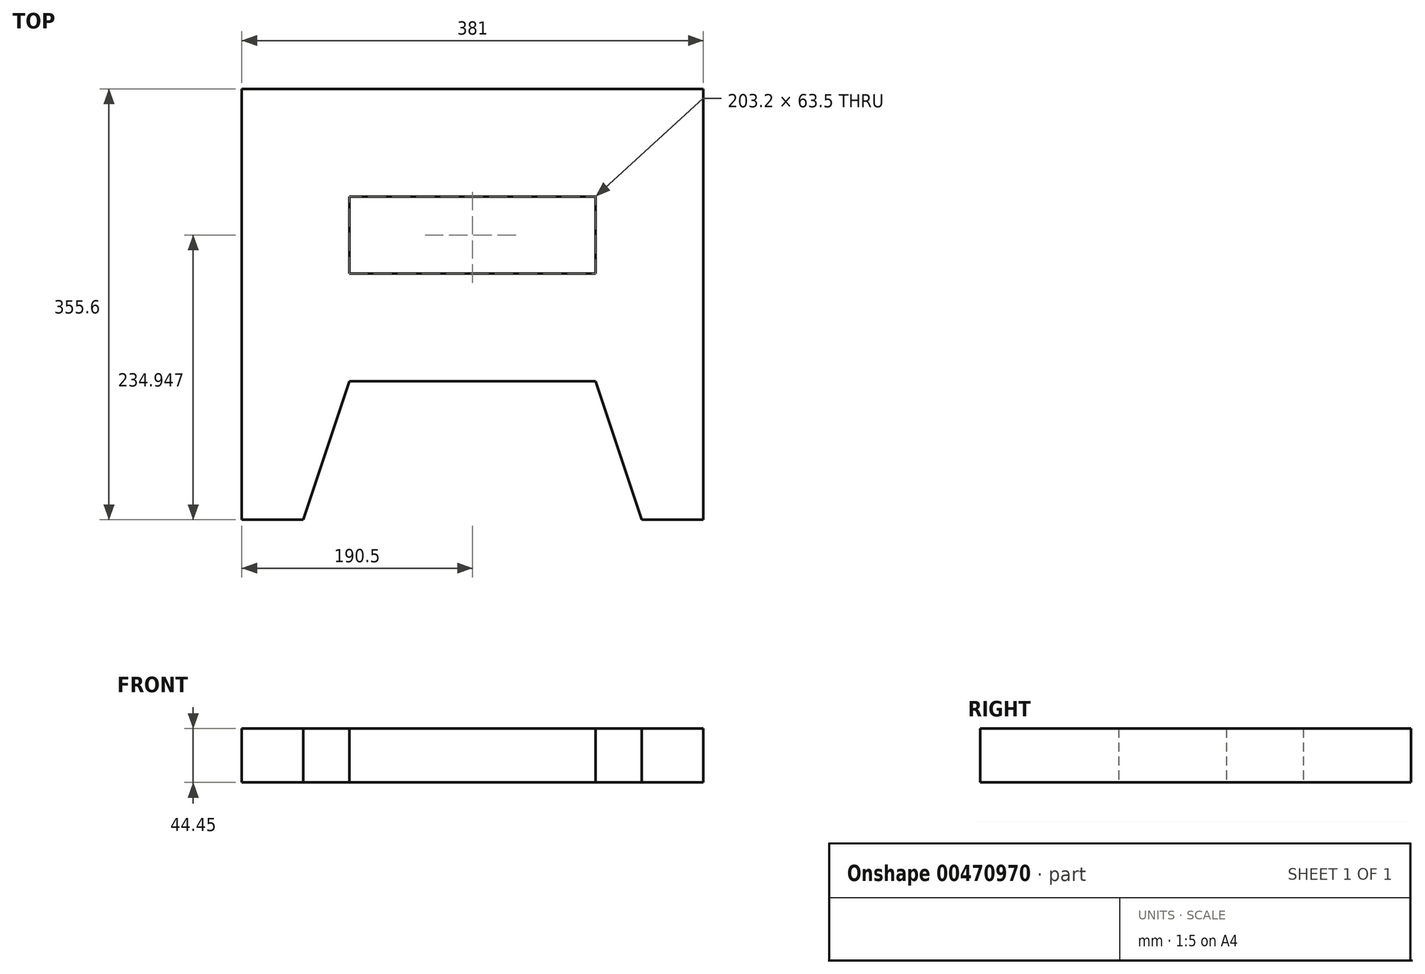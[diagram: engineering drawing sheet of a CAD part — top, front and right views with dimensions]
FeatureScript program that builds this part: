
annotation { "Feature Type Name" : "Feature", "Feature Type Description" : "" }
export const myFeature = defineFeature(function(context is Context, id is Id, definition is map)
    precondition{}
    {
        {
            var Q0;
            Q0=qCreatedBy(makeId("Top.planeOp"),FACE);
            var sketch = newSketch(context, id + "F0", { "sketchPlane" : qUnion([Q0])});
            skLineSegment(sketch, "E0.bottom", {"start": v(-101.6, 140.89) * mm, "end": v(-190.5, 140.89) * mm});
            skLineSegment(sketch, "E0.top", {"start": v(-190.5, -214.71) * mm, "end": v(-101.6, -214.71) * mm});
            skLineSegment(sketch, "E0.left", {"start": v(-190.5, 140.89) * mm, "end": v(-190.5, -214.71) * mm});
            skLineSegment(sketch, "E0.right", {"start": v(-101.6, 140.89) * mm, "end": v(-101.6, -214.71) * mm});
            skLineSegment(sketch, "E1.MirrorCS", {"start": v(101.6, 140.89) * mm, "end": v(190.5, 140.89) * mm});
            skLineSegment(sketch, "E2.MirrorCS", {"start": v(101.6, 140.89) * mm, "end": v(101.6, -214.71) * mm});
            skLineSegment(sketch, "E3.MirrorCS", {"start": v(190.5, -214.71) * mm, "end": v(101.6, -214.71) * mm});
            skLineSegment(sketch, "E4.MirrorCS", {"start": v(190.5, 140.89) * mm, "end": v(190.5, -214.71) * mm});
            skLineSegment(sketch, "E5.bottom", {"start": v(-101.6, 140.89) * mm, "end": v(101.6, 140.89) * mm});
            skLineSegment(sketch, "E5.top", {"start": v(-101.6, 51.99) * mm, "end": v(101.6, 51.99) * mm});
            skLineSegment(sketch, "E5.left", {"start": v(-101.6, 140.89) * mm, "end": v(-101.6, 51.99) * mm});
            skLineSegment(sketch, "E5.right", {"start": v(101.6, 140.89) * mm, "end": v(101.6, 51.99) * mm});
            skLineSegment(sketch, "E6.bottom", {"start": v(-101.6, -11.51) * mm, "end": v(101.6, -11.51) * mm});
            skLineSegment(sketch, "E6.top", {"start": v(-101.6, -100.41) * mm, "end": v(101.6, -100.41) * mm});
            skLineSegment(sketch, "E6.left", {"start": v(-101.6, -11.51) * mm, "end": v(-101.6, -100.41) * mm});
            skLineSegment(sketch, "E6.right", {"start": v(101.6, -11.51) * mm, "end": v(101.6, -100.41) * mm});
            skLineSegment(sketch, "E7", {"start": v(101.6, -100.41) * mm, "end": v(139.7, -214.71) * mm});
            skLineSegment(sketch, "E8", {"start": v(-101.6, -100.41) * mm, "end": v(-139.7, -214.71) * mm});
            skSolve(sketch);
        }
        {
            var Q0;
            Q0=makeQuery(id+"F0.imprint","IMPRINT",FACE,{"disambiguationData":[TD([[makeQuery(id+"F0.imprint","IMPRINT",EDGE,{"derivedFrom":sQuery(id+"F0.wireOp",EDGE,"E5.bottom")}),-1.0]])]});
            var Q1;
            Q1=makeQuery(id+"F0.imprint","IMPRINT",FACE,{"disambiguationData":[TD([[makeQuery(id+"F0.imprint","IMPRINT",EDGE,{"derivedFrom":sQuery(id+"F0.wireOp",EDGE,"E0.bottom")}),1.0]])]});
            var Q2;
            Q2=makeQuery(id+"F0.imprint","IMPRINT",FACE,{"disambiguationData":[TD([[makeQuery(id+"F0.imprint","IMPRINT",EDGE,{"derivedFrom":sQuery(id+"F0.wireOp",EDGE,"E1.MirrorCS")}),-1.0]])]});
            var Q3;
            Q3=makeQuery(id+"F0.imprint","IMPRINT",FACE,{"disambiguationData":[TD([[makeQuery(id+"F0.imprint","IMPRINT",EDGE,{"derivedFrom":sQuery(id+"F0.wireOp",EDGE,"E6.bottom")}),-1.0]])]});
            extrude(context, id + "F1", {"entities" : qUnion([Q0, Q1, Q2, Q3]), "depth" : 44.45 * mm});
        }
    });
